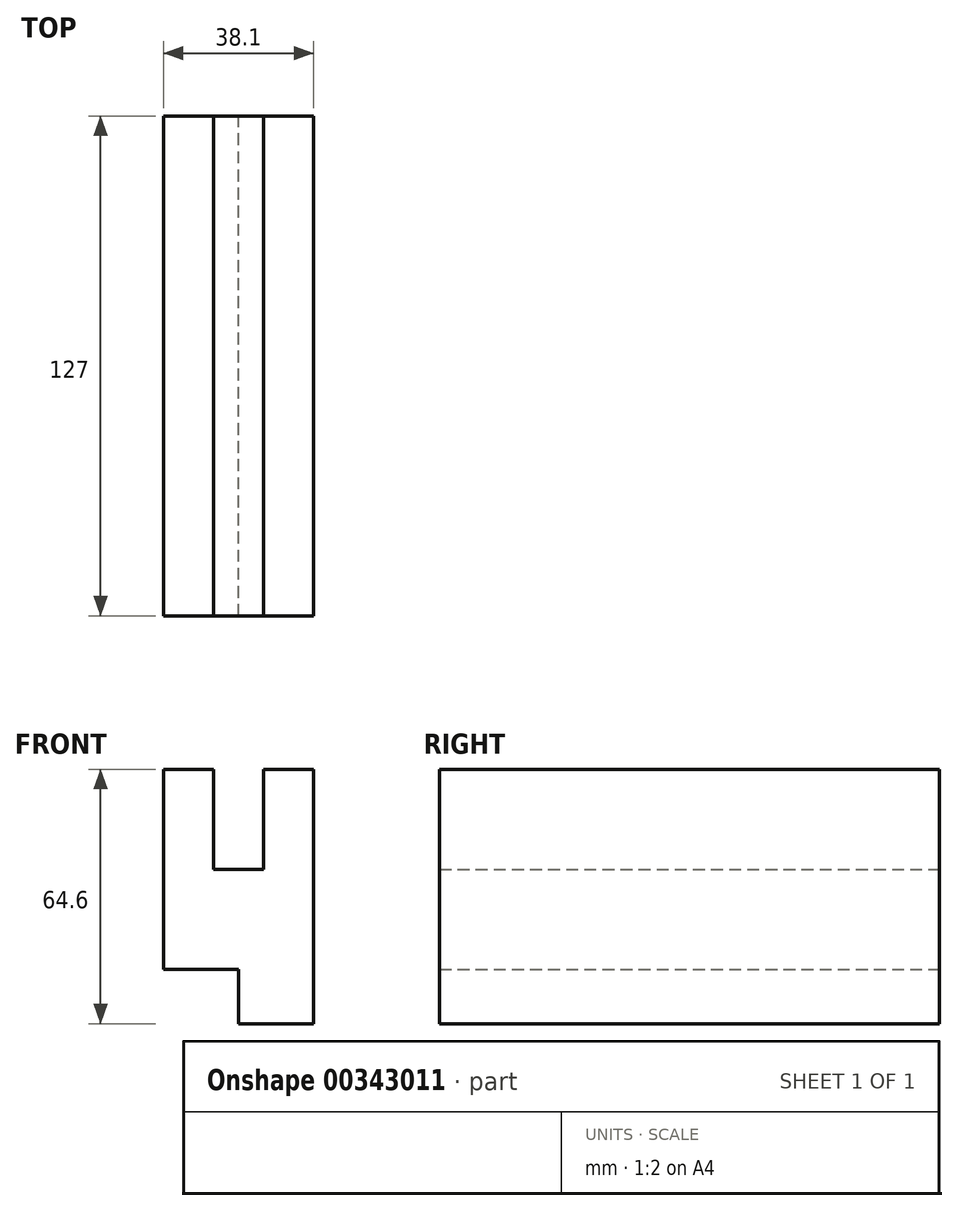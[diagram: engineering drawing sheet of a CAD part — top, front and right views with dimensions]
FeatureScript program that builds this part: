
annotation { "Feature Type Name" : "Feature", "Feature Type Description" : "" }
export const myFeature = defineFeature(function(context is Context, id is Id, definition is map)
    precondition{}
    {
        {
            var Q0;
            Q0=qCreatedBy(makeId("Front.planeOp"),FACE);
            var sketch = newSketch(context, id + "F0", { "sketchPlane" : qUnion([Q0])});
            skLineSegment(sketch, "E0", {"start": v(-38.1, 57.84) * mm, "end": v(-38.1, 32.44) * mm});
            skLineSegment(sketch, "E1", {"start": v(-38.1, 57.84) * mm, "end": v(-25.4, 57.84) * mm});
            skLineSegment(sketch, "E2", {"start": v(-25.4, 57.84) * mm, "end": v(-25.4, 32.44) * mm});
            skLineSegment(sketch, "E3", {"start": v(-25.4, 32.44) * mm, "end": v(-12.7, 32.44) * mm});
            skLineSegment(sketch, "E4", {"start": v(-12.7, 32.44) * mm, "end": v(-12.7, 57.84) * mm});
            skLineSegment(sketch, "E5", {"start": v(-12.7, 57.84) * mm, "end": v(0, 57.84) * mm});
            skLineSegment(sketch, "E6", {"start": v(0, 57.84) * mm, "end": v(0, -6.76) * mm});
            skLineSegment(sketch, "E7", {"start": v(0, -6.76) * mm, "end": v(-19.05, -6.76) * mm});
            skLineSegment(sketch, "E8", {"start": v(-19.05, -6.76) * mm, "end": v(-19.05, 7.04) * mm});
            skLineSegment(sketch, "E9", {"start": v(-19.05, 7.04) * mm, "end": v(-38.1, 7.04) * mm});
            skLineSegment(sketch, "E10", {"start": v(-38.1, 32.44) * mm, "end": v(-38.1, 7.04) * mm});
            skSolve(sketch);
        }
        {
            var Q0;
            Q0 = qSketchRegion(id + "F0", true);
            extrude(context, id + "F1", {"entities" : qUnion([Q0]), "depth" : 127 * mm});
        }
    });
